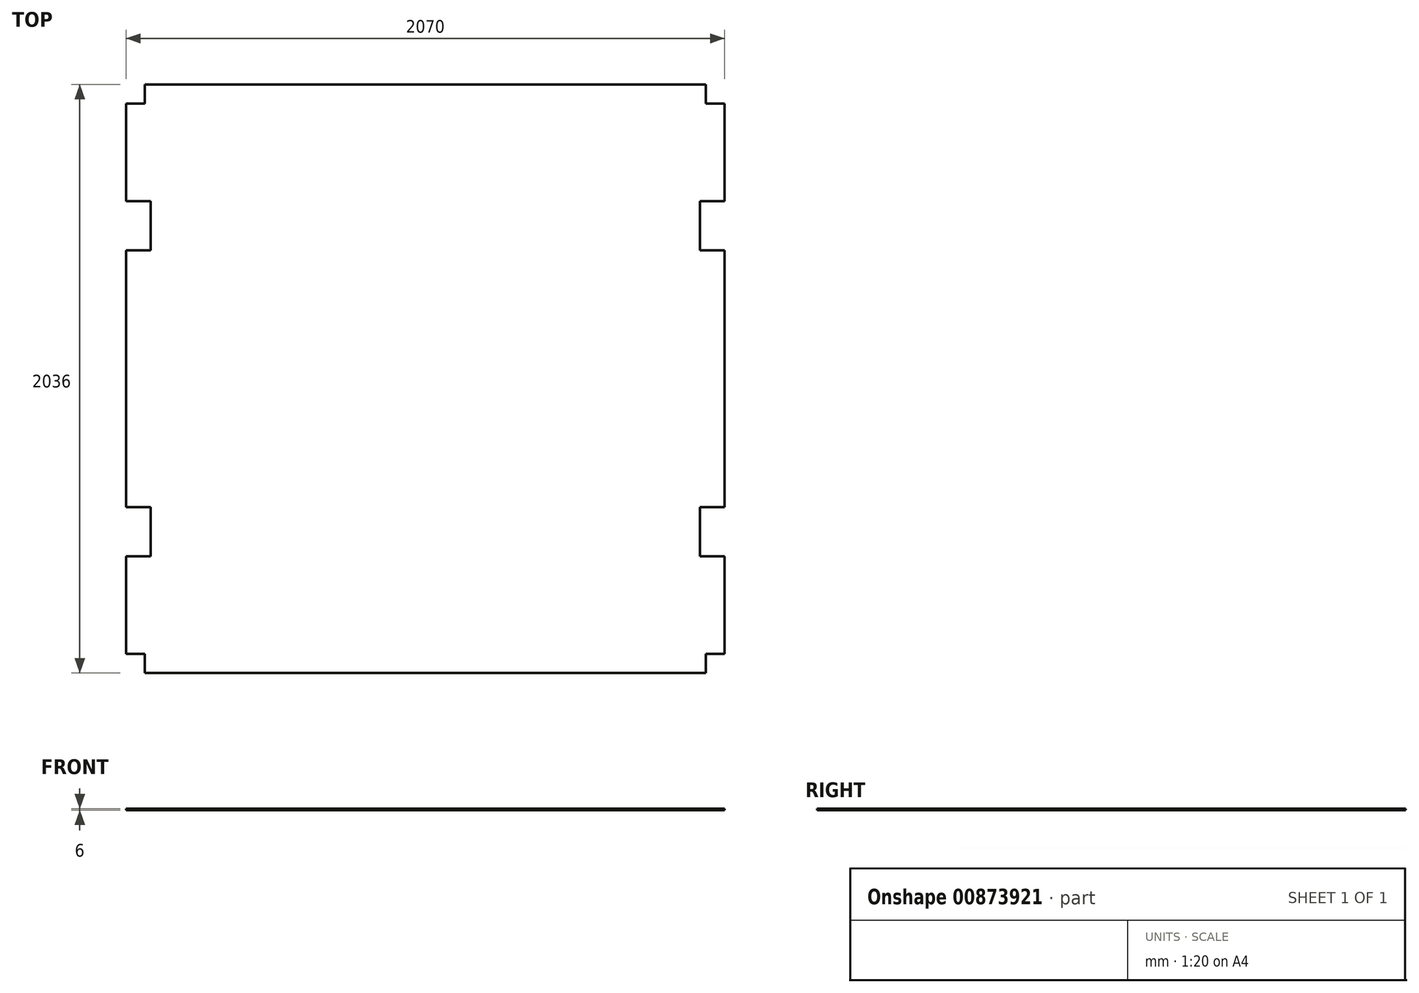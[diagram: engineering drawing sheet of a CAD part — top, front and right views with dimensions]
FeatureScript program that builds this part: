
annotation { "Feature Type Name" : "Feature", "Feature Type Description" : "" }
export const myFeature = defineFeature(function(context is Context, id is Id, definition is map)
    precondition{}
    {
        {
            var Q0;
            Q0=qCreatedBy(makeId("Top.planeOp"),FACE);
            var sketch = newSketch(context, id + "F0", { "sketchPlane" : qUnion([Q0])});
            skLineSegment(sketch, "E0.bottom", {"start": v(1035, 1018) * mm, "end": v(-1035, 1018) * mm});
            skLineSegment(sketch, "E0.top", {"start": v(1035, -1018) * mm, "end": v(-1035, -1018) * mm});
            skLineSegment(sketch, "E0.left", {"start": v(1035, 1018) * mm, "end": v(1035, -1018) * mm});
            skLineSegment(sketch, "E0.right", {"start": v(-1035, 1018) * mm, "end": v(-1035, -1018) * mm});
            skPoint(sketch, "E0.middle", {"position": v(0, 0) * mm});
            skSolve(sketch);
        }
        {
            var Q0;
            Q0=makeQuery(id+"F0.imprint","IMPRINT",FACE,{"disambiguationData":[TD([[makeQuery(id+"F0.imprint","IMPRINT",EDGE,{"derivedFrom":sQuery(id+"F0.wireOp",EDGE,"E0.bottom")}),1.0]])]});
            extrude(context, id + "F1", {"entities" : qUnion([Q0]), "depth" : 6 * mm, "offsetDistance" : 25 * mm, "symmetric" : true});
        }
        {
            var Q0;
            Q0=makeQuery(id+"F1.opExtrude","CAP_FACE",FACE,{"disambiguationData":[OSD([sQuery(id+"F0.wireOp",EDGE,"E0.bottom"),sQuery(id+"F0.wireOp",EDGE,"E0.top"),sQuery(id+"F0.wireOp",EDGE,"E0.left"),sQuery(id+"F0.wireOp",EDGE,"E0.right")])],"isStart":false});
            var sketch = newSketch(context, id + "F2", { "sketchPlane" : qUnion([Q0])});
            skLineSegment(sketch, "E1.bottom", {"start": v(-1035, 1018) * mm, "end": v(-970, 1018) * mm});
            skLineSegment(sketch, "E1.top", {"start": v(-1035, 953) * mm, "end": v(-970, 953) * mm});
            skLineSegment(sketch, "E1.left", {"start": v(-1035, 1018) * mm, "end": v(-1035, 953) * mm});
            skLineSegment(sketch, "E1.right", {"start": v(-970, 1018) * mm, "end": v(-970, 953) * mm});
            skLineSegment(sketch, "E2", {"start": v(-1035, 1018) * mm, "end": v(-1035, 530) * mm, "construction": true});
            skLineSegment(sketch, "E3.bottom", {"start": v(-950, 615) * mm, "end": v(-1120, 615) * mm});
            skLineSegment(sketch, "E3.top", {"start": v(-950, 445) * mm, "end": v(-1120, 445) * mm});
            skLineSegment(sketch, "E3.left", {"start": v(-950, 615) * mm, "end": v(-950, 445) * mm});
            skLineSegment(sketch, "E3.right", {"start": v(-1120, 615) * mm, "end": v(-1120, 445) * mm});
            skPoint(sketch, "E3.middle", {"position": v(-1035, 530) * mm});
            skLineSegment(sketch, "E4.MirrorCS", {"start": v(-1035, -1018) * mm, "end": v(-970, -1018) * mm});
            skLineSegment(sketch, "E5.MirrorCS", {"start": v(-1035, -953) * mm, "end": v(-970, -953) * mm});
            skLineSegment(sketch, "E6.MirrorCS", {"start": v(-1035, -1018) * mm, "end": v(-1035, -953) * mm});
            skLineSegment(sketch, "E7.MirrorCS", {"start": v(-970, -1018) * mm, "end": v(-970, -953) * mm});
            skLineSegment(sketch, "E8.MirrorCS", {"start": v(-950, -445) * mm, "end": v(-1120, -445) * mm});
            skLineSegment(sketch, "E9.MirrorCS", {"start": v(-950, -615) * mm, "end": v(-950, -445) * mm});
            skLineSegment(sketch, "E10.MirrorCS", {"start": v(-1120, -615) * mm, "end": v(-1120, -445) * mm});
            skPoint(sketch, "E11.MirrorP", {"position": v(-1035, -530) * mm});
            skLineSegment(sketch, "E12.MirrorCS", {"start": v(-950, -615) * mm, "end": v(-1120, -615) * mm});
            skLineSegment(sketch, "E13.MirrorCS", {"start": v(-1035, -1018) * mm, "end": v(-1035, -530) * mm, "construction": true});
            skLineSegment(sketch, "E14.MirrorCS", {"start": v(970, 1018) * mm, "end": v(970, 953) * mm});
            skLineSegment(sketch, "E15.MirrorCS", {"start": v(1035, -1018) * mm, "end": v(970, -1018) * mm});
            skLineSegment(sketch, "E16.MirrorCS", {"start": v(1035, 1018) * mm, "end": v(1035, 953) * mm});
            skLineSegment(sketch, "E17.MirrorCS", {"start": v(1035, 953) * mm, "end": v(970, 953) * mm});
            skLineSegment(sketch, "E18.MirrorCS", {"start": v(1035, -1018) * mm, "end": v(1035, -953) * mm});
            skLineSegment(sketch, "E19.MirrorCS", {"start": v(970, -1018) * mm, "end": v(970, -953) * mm});
            skLineSegment(sketch, "E20.MirrorCS", {"start": v(1035, 1018) * mm, "end": v(970, 1018) * mm});
            skLineSegment(sketch, "E21.MirrorCS", {"start": v(1035, -953) * mm, "end": v(970, -953) * mm});
            skLineSegment(sketch, "E22.MirrorCS", {"start": v(950, -615) * mm, "end": v(1120, -615) * mm});
            skLineSegment(sketch, "E23.MirrorCS", {"start": v(1120, 615) * mm, "end": v(1120, 445) * mm});
            skPoint(sketch, "E24.MirrorP", {"position": v(1035, 530) * mm});
            skLineSegment(sketch, "E25.MirrorCS", {"start": v(950, 615) * mm, "end": v(950, 445) * mm});
            skLineSegment(sketch, "E26.MirrorCS", {"start": v(950, -615) * mm, "end": v(950, -445) * mm});
            skLineSegment(sketch, "E27.MirrorCS", {"start": v(950, -445) * mm, "end": v(1120, -445) * mm});
            skLineSegment(sketch, "E28.MirrorCS", {"start": v(1120, -615) * mm, "end": v(1120, -445) * mm});
            skPoint(sketch, "E29.MirrorP", {"position": v(1035, -530) * mm});
            skLineSegment(sketch, "E30.MirrorCS", {"start": v(950, 615) * mm, "end": v(1120, 615) * mm});
            skLineSegment(sketch, "E31.MirrorCS", {"start": v(1035, 1018) * mm, "end": v(1035, 530) * mm, "construction": true});
            skLineSegment(sketch, "E32.MirrorCS", {"start": v(950, 445) * mm, "end": v(1120, 445) * mm});
            skLineSegment(sketch, "E33.MirrorCS", {"start": v(1035, -1018) * mm, "end": v(1035, -530) * mm, "construction": true});
            skSolve(sketch);
        }
        {
            var Q0;
            Q0 = qSketchRegion(id + "F2", true);
            extrude(context, id + "F3", {"entities" : qUnion([Q0]), "operationType" : NewBodyOperationType.REMOVE, "endBound" : BoundingType.THROUGH_ALL, "oppositeDirection" : true, "depth" : 25 * mm, "offsetDistance" : 25 * mm});
        }
    });
